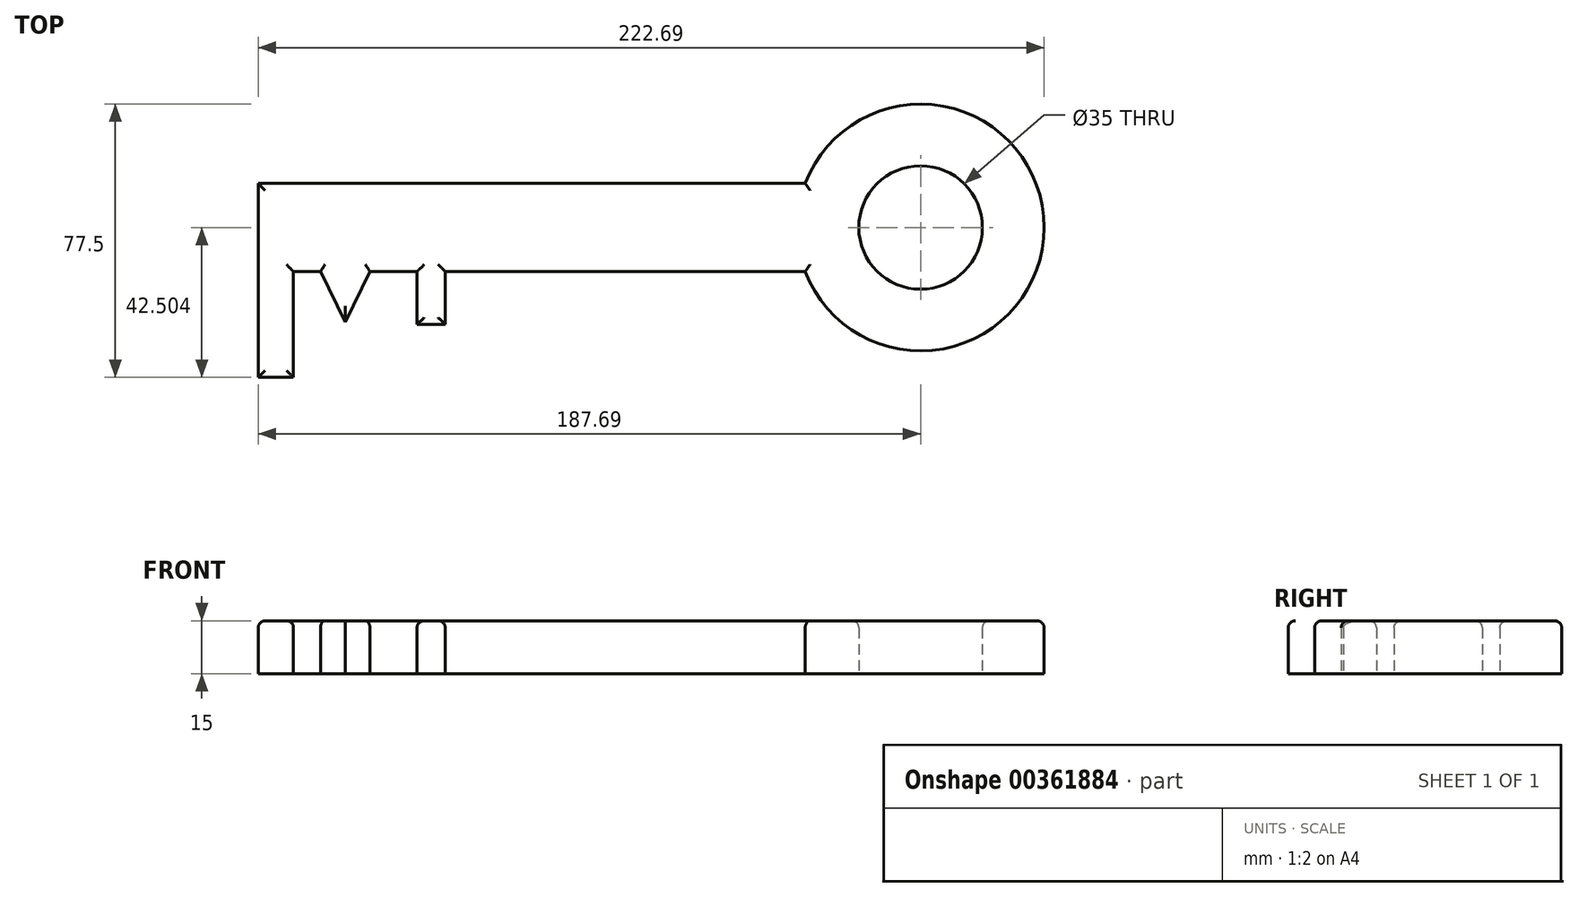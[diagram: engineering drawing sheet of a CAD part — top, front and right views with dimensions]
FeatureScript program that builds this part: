
annotation { "Feature Type Name" : "Feature", "Feature Type Description" : "" }
export const myFeature = defineFeature(function(context is Context, id is Id, definition is map)
    precondition{}
    {
        {
            var Q0;
            Q0=qCreatedBy(makeId("Top.planeOp"),FACE);
            var sketch = newSketch(context, id + "F0", { "sketchPlane" : qUnion([Q0])});
            skLineSegment(sketch, "E0.bottom", {"start": v(-76.06, 17.9) * mm, "end": v(78.94, 17.9) * mm});
            skLineSegment(sketch, "E0.top", {"start": v(-66.06, -7.1) * mm, "end": v(-58.41, -7.1) * mm});
            skLineSegment(sketch, "E0.left", {"start": v(-76.06, 17.9) * mm, "end": v(-76.06, -7.1) * mm});
            skLineSegment(sketch, "E1.top", {"start": v(-76.06, -37.1) * mm, "end": v(-66.06, -37.1) * mm});
            skLineSegment(sketch, "E1.left", {"start": v(-76.06, -7.1) * mm, "end": v(-76.06, -37.1) * mm});
            skLineSegment(sketch, "E1.right", {"start": v(-66.06, -7.1) * mm, "end": v(-66.06, -37.1) * mm});
            skLineSegment(sketch, "E2.top", {"start": v(-31.06, -22.1) * mm, "end": v(-23.06, -22.1) * mm});
            skLineSegment(sketch, "E2.left", {"start": v(-31.06, -7.1) * mm, "end": v(-31.06, -22.1) * mm});
            skLineSegment(sketch, "E2.right", {"start": v(-23.06, -7.1) * mm, "end": v(-23.06, -22.1) * mm});
            skLineSegment(sketch, "E3", {"start": v(-58.41, -7.1) * mm, "end": v(-51.41, -21.47) * mm});
            skLineSegment(sketch, "E4", {"start": v(-51.41, -21.47) * mm, "end": v(-44.41, -7.1) * mm});
            skArc(sketch, "E5", {"start": v(78.94, -7.1) * mm, "mid": v(146.63, 5.4) * mm, "end": v(78.94, 17.9) * mm});
            skCircle(sketch, "E6", {"center": v(111.63, 5.4) * mm, "radius": 17.5 * mm});
            skLineSegment(sketch, "E7.trimOffspring", {"start": v(-23.06, -7.1) * mm, "end": v(78.94, -7.1) * mm});
            skLineSegment(sketch, "E8.trimOffspring", {"start": v(-44.41, -7.1) * mm, "end": v(-31.06, -7.1) * mm});
            skSolve(sketch);
        }
        {
            var Q0;
            Q0=makeQuery(id+"F0.imprint","IMPRINT",FACE,{"disambiguationData":[TD([[makeQuery(id+"F0.imprint","IMPRINT",EDGE,{"derivedFrom":sQuery(id+"F0.wireOp",EDGE,"E0.bottom")}),-1.0]])]});
            extrude(context, id + "F1", {"entities" : qUnion([Q0]), "depth" : 15 * mm});
        }
        {
            var Q0;
            Q0=makeQuery(id+"F1.opExtrude","CAP_FACE",FACE,{"disambiguationData":[OSD([sQuery(id+"F0.wireOp",EDGE,"E0.bottom"),sQuery(id+"F0.wireOp",EDGE,"E0.top"),sQuery(id+"F0.wireOp",EDGE,"E0.left"),sQuery(id+"F0.wireOp",EDGE,"E1.top"),sQuery(id+"F0.wireOp",EDGE,"E1.left"),sQuery(id+"F0.wireOp",EDGE,"E1.right"),sQuery(id+"F0.wireOp",EDGE,"E2.top"),sQuery(id+"F0.wireOp",EDGE,"E2.left"),sQuery(id+"F0.wireOp",EDGE,"E2.right"),sQuery(id+"F0.wireOp",EDGE,"E3"),sQuery(id+"F0.wireOp",EDGE,"E4"),sQuery(id+"F0.wireOp",EDGE,"E5"),sQuery(id+"F0.wireOp",EDGE,"E6"),sQuery(id+"F0.wireOp",EDGE,"E7.trimOffspring"),sQuery(id+"F0.wireOp",EDGE,"E8.trimOffspring")])],"isStart":false});
            fillet(context, id + "F2", {"entities" : qUnion([Q0]), "radius" : 2 * mm, "tangentPropagation" : true, "allowEdgeOverflow" : false});
        }
    });
